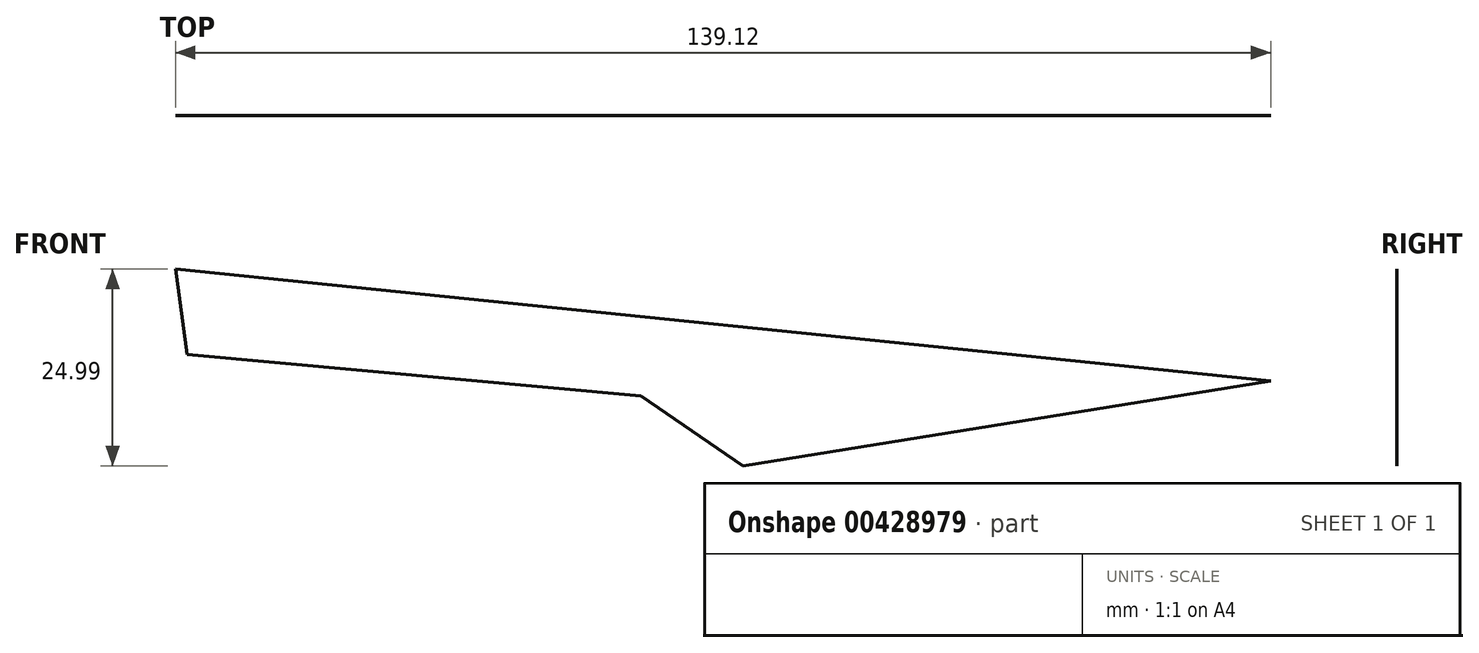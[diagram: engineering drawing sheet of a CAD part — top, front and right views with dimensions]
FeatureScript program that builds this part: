
annotation { "Feature Type Name" : "Feature", "Feature Type Description" : "" }
export const myFeature = defineFeature(function(context is Context, id is Id, definition is map)
    precondition{}
    {
        {
            var Q0;
            Q0=qCreatedBy(makeId("Front.planeOp"),FACE);
            var sketch = newSketch(context, id + "F0", { "sketchPlane" : qUnion([Q0])});
            skLineSegment(sketch, "E0", {"start": v(-67.28, 42.53) * mm, "end": v(71.84, 28.35) * mm});
            skLineSegment(sketch, "E1", {"start": v(71.84, 28.35) * mm, "end": v(4.8, 17.54) * mm});
            skLineSegment(sketch, "E2", {"start": v(4.8, 17.54) * mm, "end": v(-8.17, 26.43) * mm});
            skLineSegment(sketch, "E3", {"start": v(-8.17, 26.43) * mm, "end": v(-65.83, 31.72) * mm});
            skLineSegment(sketch, "E4", {"start": v(-65.83, 31.72) * mm, "end": v(-67.28, 42.53) * mm});
            skSolve(sketch);
        }
        {
            var Q0;
            Q0 = qSketchRegion(id + "F0", true);
            extrude(context, id + "F1", {"entities" : qUnion([Q0]), "depth" : 3 / 812.8 * mm});
        }
    });
